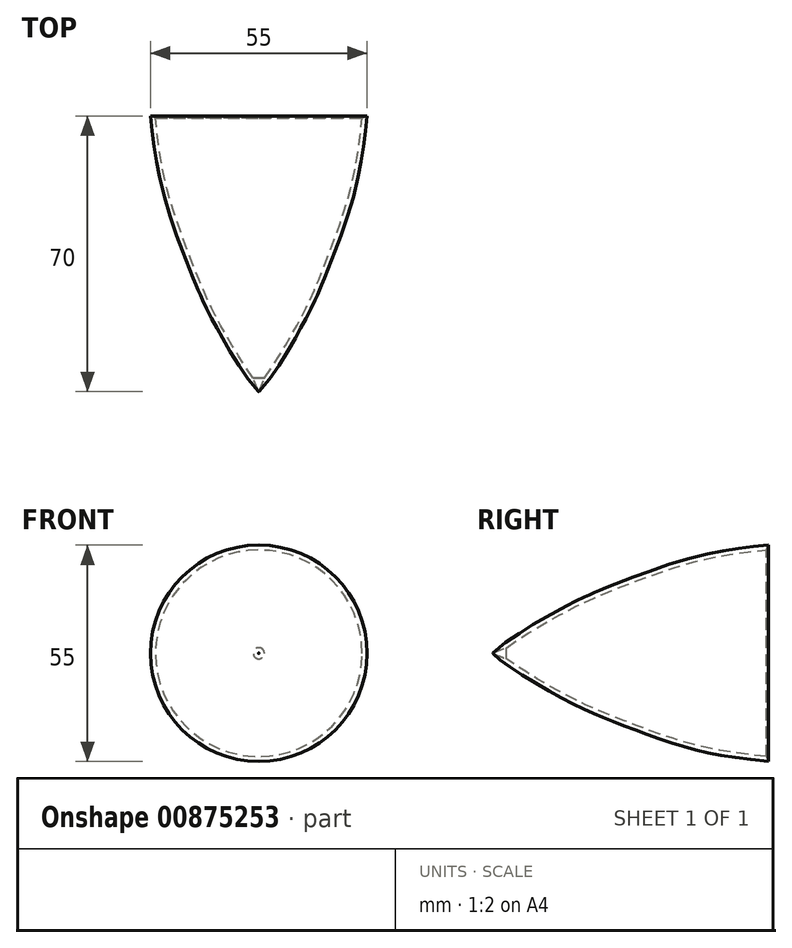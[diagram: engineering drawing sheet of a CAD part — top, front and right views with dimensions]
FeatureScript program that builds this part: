
annotation { "Feature Type Name" : "Feature", "Feature Type Description" : "" }
export const myFeature = defineFeature(function(context is Context, id is Id, definition is map)
    precondition{}
    {
        {
            var Q0;
            Q0=qCreatedBy(makeId("Right.planeOp"),FACE);
            var sketch = newSketch(context, id + "F0", { "sketchPlane" : qUnion([Q0])});
            skFitSpline(sketch, "E0", {"points": [v(0, 27.5) * mm, v(-22.73, 23.38) * mm, v(-39.39, 17.38) * mm, v(-52.64, 11.34) * mm, v(-70.1, 0) * mm], "startDerivative": vector(-109.98, -11.05) * mm, "endDerivative": vector(-28.26, -30.77) * mm});
            skFitSpline(sketch, "E1.0", {"points": [v(0.12, 26.3) * mm, v(-2.16, 26.08) * mm, v(-6.3, 25.6) * mm, v(-11.58, 24.82) * mm, v(-15.45, 24.05) * mm, v(-18.38, 23.35) * mm, v(-20.55, 22.77) * mm, v(-22.72, 22.14) * mm, v(-24.93, 21.44) * mm, v(-27.15, 20.7) * mm, v(-30.11, 19.66) * mm, v(-33.03, 18.57) * mm, v(-35.82, 17.5) * mm, v(-37.83, 16.7) * mm, v(-39.74, 15.95) * mm, v(-41.55, 15.22) * mm, v(-43.3, 14.5) * mm, v(-45.05, 13.74) * mm, v(-46.84, 12.92) * mm, v(-48.72, 12.02) * mm, v(-50.4, 11.17) * mm, v(-51.83, 10.41) * mm, v(-53.33, 9.6) * mm, v(-55.32, 8.5) * mm, v(-57.8, 7.07) * mm, v(-60.26, 5.6) * mm, v(-62.64, 4.11) * mm, v(-64.82, 2.67) * mm, v(-66.73, 1.32) * mm, v(-68.27, 0.11) * mm, v(-68.97, -0.55) * mm, v(-69.21, -0.81) * mm]});
            skLineSegment(sketch, "E2", {"start": v(0, 27.5) * mm, "end": v(-0.57, 26.24) * mm});
            skLineSegment(sketch, "E3", {"start": v(-55, 0) * mm, "end": v(0, 0) * mm, "construction": true});
            skLineSegment(sketch, "E4", {"start": v(-66.54, 1.44) * mm, "end": v(-70, 0.1) * mm});
            skPoint(sketch, "E5.orphan", {"position": v(-70, 0.1) * mm});
            skSolve(sketch);
        }
        {
            var Q0;
            Q0=makeQuery(id+"F0.imprint","IMPRINT",FACE,{"disambiguationData":[TD([[makeQuery(id+"F0.imprint","IMPRINT",EDGE,{"derivedFrom":sQuery(id+"F0.wireOp",EDGE,"E0")}),1.0]])]});
            var Q1;
            Q1=sQuery(id+"F0.wireOp",EDGE,"E3");
            revolve(context, id + "F1", {"surfaceOperationType" : NewSurfaceOperationType.NEW, "entities" : qUnion([Q0]), "axis" : qUnion([Q1]), "revolveType" : RevolveType.FULL});
        }
    });
